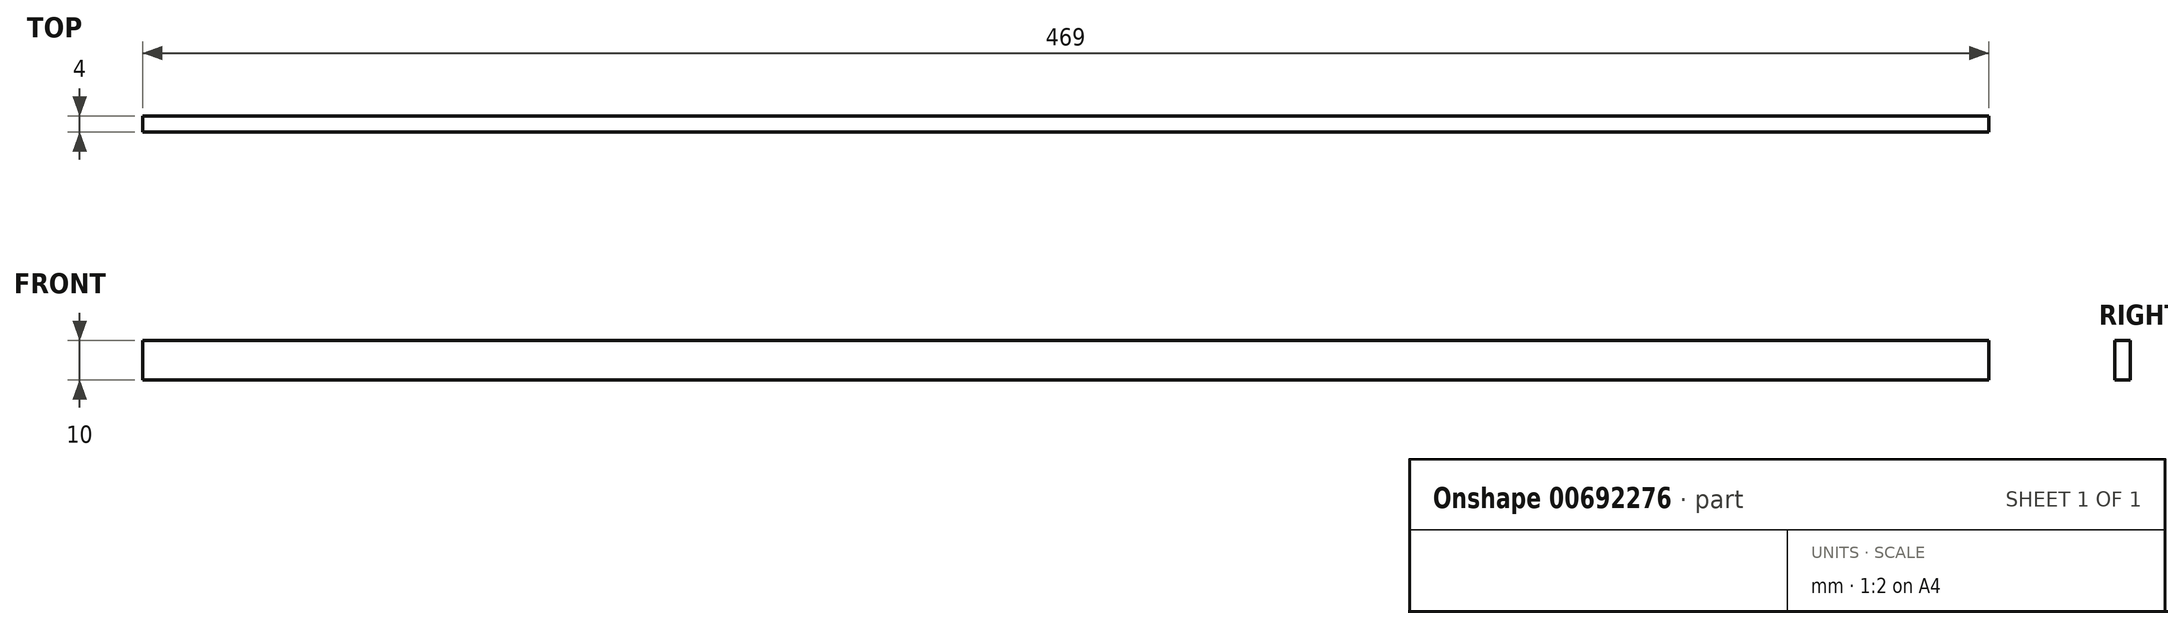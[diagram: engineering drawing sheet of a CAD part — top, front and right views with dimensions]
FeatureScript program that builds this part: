
annotation { "Feature Type Name" : "Feature", "Feature Type Description" : "" }
export const myFeature = defineFeature(function(context is Context, id is Id, definition is map)
    precondition{}
    {
        {
            var Q0;
            Q0=qCreatedBy(makeId("Top.planeOp"),FACE);
            var sketch = newSketch(context, id + "F0", { "sketchPlane" : qUnion([Q0])});
            skLineSegment(sketch, "E0.bottom", {"start": v(0, 0) * mm, "end": v(469, 0) * mm});
            skLineSegment(sketch, "E0.top", {"start": v(0, 4) * mm, "end": v(469, 4) * mm});
            skLineSegment(sketch, "E0.left", {"start": v(0, 0) * mm, "end": v(0, 4) * mm});
            skLineSegment(sketch, "E0.right", {"start": v(469, 0) * mm, "end": v(469, 4) * mm});
            skSolve(sketch);
        }
        {
            var Q0;
            Q0 = qSketchRegion(id + "F0", true);
            extrude(context, id + "F1", {"entities" : qUnion([Q0]), "depth" : 10 * mm, "offsetDistance" : 25.4 * mm});
        }
    });
